# Revit family: QF_Hallde_MT-x_RG-350
name_source: partatom
category: Specialty Equipment
revit_build: Autodesk Revit 2018 (Build: 20181015_0930(x64)
units: mm (PartAtom-declared; Revit-internal decimal feet)

## family parameters
Always vertical = Yes
Cut with Voids When Loaded = No
OmniClass Number = 23.40.40.00
OmniClass Title = Food Service Equipment and Furnishings
Part Type = Normal
Room Calculation Point = No
Round Connector Dimension = Use Diameter
Shared = No
Work Plane-Based = No

## types (3) — shared parameters
Assembly Code = E1090300
Depth = 603 mm
Foodservice Equipment Identifier = Yes
Height = 615 mm  [stored 2.01772 ft]
Manufacturer = Hallde AB
Width = 530 mm  [stored 1.73885 ft]
zero-valued in all types: Weight in Pounds

## per-type parameters (varying)
| type | Description | Tray Height |
| MT-H_RG-350 | Machine Table High Position & RG-350 | 600 mm |
| MT-M_RG-350 | Machine Table Mid Position & RG-350 | 495 mm  [stored 1.62402 ft] |
| MT-L_RG-350 | Machine Table Low Position & RG-350 | 390 mm  [stored 1.27953 ft] |

note: column(s) folded — value = type name in every type: Model

note: [stored X ft] marks values corroborated as IEEE doubles in the binary element streams (Revit-internal decimal feet)

## geometry (parser evidence)
native form markers: Blend x8, Sweep x9
no freeform markers — native parametric forms only
